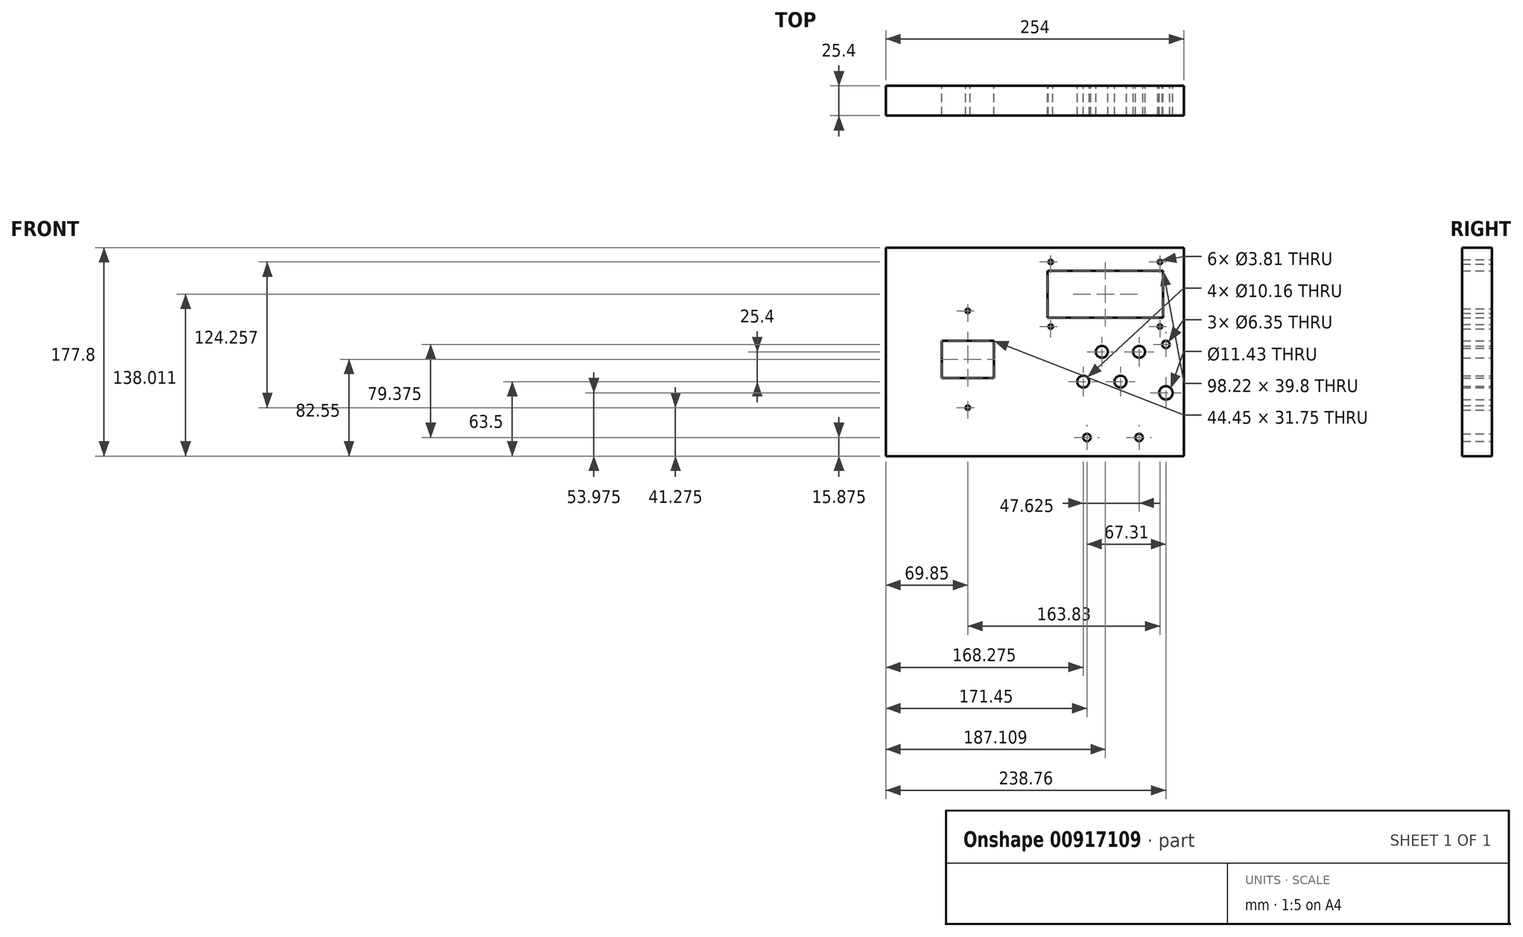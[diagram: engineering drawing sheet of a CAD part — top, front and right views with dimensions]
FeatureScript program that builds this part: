
annotation { "Feature Type Name" : "Feature", "Feature Type Description" : "" }
export const myFeature = defineFeature(function(context is Context, id is Id, definition is map)
    precondition{}
    {
        {
            var Q0;
            Q0=qCreatedBy(makeId("Front.planeOp"),FACE);
            var sketch = newSketch(context, id + "F0", { "sketchPlane" : qUnion([Q0])});
            skLineSegment(sketch, "E0.bottom", {"start": v(0, 0) * mm, "end": v(254, 0) * mm});
            skLineSegment(sketch, "E0.top", {"start": v(0, -177.8) * mm, "end": v(254, -177.8) * mm});
            skLineSegment(sketch, "E0.left", {"start": v(0, 0) * mm, "end": v(0, -177.8) * mm});
            skLineSegment(sketch, "E0.right", {"start": v(254, 0) * mm, "end": v(254, -177.8) * mm});
            skLineSegment(sketch, "E1.bottom", {"start": v(0, 0) * mm, "end": v(17.78, 0) * mm});
            skLineSegment(sketch, "E1.top", {"start": v(5.08, -17.78) * mm, "end": v(17.78, -17.78) * mm, "construction": true});
            skLineSegment(sketch, "E1.left", {"start": v(0, 0) * mm, "end": v(0, -17.78) * mm});
            skLineSegment(sketch, "E1.right", {"start": v(17.78, -5.08) * mm, "end": v(17.78, -17.78) * mm, "construction": true});
            skLineSegment(sketch, "E2.bottom", {"start": v(254, 0) * mm, "end": v(236.22, 0) * mm});
            skLineSegment(sketch, "E2.top", {"start": v(248.92, -17.78) * mm, "end": v(236.22, -17.78) * mm, "construction": true});
            skLineSegment(sketch, "E2.left", {"start": v(254, 0) * mm, "end": v(254, -17.78) * mm});
            skLineSegment(sketch, "E2.right", {"start": v(236.22, -5.08) * mm, "end": v(236.22, -17.78) * mm, "construction": true});
            skLineSegment(sketch, "E3.bottom", {"start": v(0, -177.8) * mm, "end": v(17.78, -177.8) * mm});
            skLineSegment(sketch, "E3.top", {"start": v(5.08, -160.02) * mm, "end": v(17.78, -160.02) * mm, "construction": true});
            skLineSegment(sketch, "E3.left", {"start": v(0, -177.8) * mm, "end": v(0, -160.02) * mm});
            skLineSegment(sketch, "E3.right", {"start": v(17.78, -172.72) * mm, "end": v(17.78, -160.02) * mm, "construction": true});
            skLineSegment(sketch, "E4.bottom", {"start": v(254, -177.8) * mm, "end": v(236.22, -177.8) * mm});
            skLineSegment(sketch, "E4.top", {"start": v(248.92, -160.02) * mm, "end": v(236.22, -160.02) * mm, "construction": true});
            skLineSegment(sketch, "E4.left", {"start": v(254, -177.8) * mm, "end": v(254, -160.02) * mm});
            skLineSegment(sketch, "E4.right", {"start": v(236.22, -172.72) * mm, "end": v(236.22, -160.02) * mm, "construction": true});
            skLineSegment(sketch, "E5.bottom", {"start": v(0, 0) * mm, "end": v(139.7, 0) * mm});
            skLineSegment(sketch, "E5.top", {"start": v(0, -177.8) * mm, "end": v(139.7, -177.8) * mm});
            skLineSegment(sketch, "E5.right", {"start": v(139.7, -69.85) * mm, "end": v(139.7, -177.8) * mm, "construction": true});
            skCircle(sketch, "E6", {"center": v(69.85, -136.53) * mm, "radius": 1.9 * mm});
            skCircle(sketch, "E7", {"center": v(69.85, -53.97) * mm, "radius": 1.9 * mm});
            skLineSegment(sketch, "E8.bottom", {"start": v(254, -177.8) * mm, "end": v(228.6, -177.8) * mm});
            skLineSegment(sketch, "E8.top", {"start": v(254, -95.25) * mm, "end": v(228.6, -95.25) * mm, "construction": true});
            skLineSegment(sketch, "E8.left", {"start": v(254, -177.8) * mm, "end": v(254, -95.25) * mm});
            skLineSegment(sketch, "E9.bottom", {"start": v(139.7, -177.8) * mm, "end": v(228.6, -177.8) * mm});
            skLineSegment(sketch, "E9.top", {"start": v(139.7, -146.05) * mm, "end": v(228.6, -146.05) * mm, "construction": true});
            skLineSegment(sketch, "E9.left", {"start": v(139.7, -177.8) * mm, "end": v(139.7, -146.05) * mm});
            skLineSegment(sketch, "E9.right", {"start": v(228.6, -177.8) * mm, "end": v(228.6, -146.05) * mm, "construction": true});
            skLineSegment(sketch, "E10", {"start": v(139.7, -127) * mm, "end": v(228.6, -127) * mm, "construction": true});
            skPoint(sketch, "E11.endSnap0", {"position": v(254, -88.9) * mm});
            skLineSegment(sketch, "E12", {"start": v(228.6, -95.25) * mm, "end": v(228.6, -69.85) * mm, "construction": true});
            skLineSegment(sketch, "E13.left", {"start": v(236.22, -9.73) * mm, "end": v(236.22, -69.85) * mm});
            skLineSegment(sketch, "E14.bottom", {"start": v(5.08, -5.08) * mm, "end": v(248.92, -5.08) * mm, "construction": true});
            skLineSegment(sketch, "E14.top", {"start": v(5.08, -172.72) * mm, "end": v(248.92, -172.72) * mm, "construction": true});
            skLineSegment(sketch, "E14.left", {"start": v(5.08, -5.08) * mm, "end": v(5.08, -172.72) * mm, "construction": true});
            skLineSegment(sketch, "E14.right", {"start": v(248.92, -5.08) * mm, "end": v(248.92, -172.72) * mm, "construction": true});
            skCircle(sketch, "E15", {"center": v(140.54, -12.27) * mm, "radius": 1.9 * mm});
            skCircle(sketch, "E16", {"center": v(233.68, -12.27) * mm, "radius": 1.9 * mm});
            skCircle(sketch, "E17", {"center": v(233.68, -67.3) * mm, "radius": 1.9 * mm});
            skCircle(sketch, "E18", {"center": v(140.54, -67.3) * mm, "radius": 1.9 * mm});
            skLineSegment(sketch, "E19", {"start": v(138, -59.7) * mm, "end": v(236.22, -59.69) * mm});
            skLineSegment(sketch, "E20", {"start": v(138, -19.89) * mm, "end": v(236.22, -19.89) * mm});
            skLineSegment(sketch, "E21", {"start": v(69.85, -53.97) * mm, "end": v(69.85, -136.53) * mm, "construction": true});
            skLineSegment(sketch, "E22.bottom", {"start": v(47.62, -79.37) * mm, "end": v(92.07, -79.37) * mm});
            skLineSegment(sketch, "E22.top", {"start": v(47.62, -111.12) * mm, "end": v(92.07, -111.12) * mm});
            skLineSegment(sketch, "E22.left", {"start": v(47.62, -79.37) * mm, "end": v(47.62, -111.12) * mm});
            skLineSegment(sketch, "E22.right", {"start": v(92.07, -79.37) * mm, "end": v(92.07, -111.12) * mm});
            skCircle(sketch, "E23", {"center": v(215.9, -88.9) * mm, "radius": 5.08 * mm});
            skCircle(sketch, "E24", {"center": v(200.03, -114.3) * mm, "radius": 5.08 * mm});
            skCircle(sketch, "E25", {"center": v(168.28, -114.3) * mm, "radius": 5.08 * mm});
            skCircle(sketch, "E26", {"center": v(184.15, -88.9) * mm, "radius": 5.08 * mm});
            skLineSegment(sketch, "E27", {"start": v(236.22, -160.02) * mm, "end": v(228.6, -160.02) * mm, "construction": true});
            skLineSegment(sketch, "E28", {"start": v(138, -69.85) * mm, "end": v(254, -69.85) * mm, "construction": true});
            skLineSegment(sketch, "E29", {"start": v(138, -9.73) * mm, "end": v(236.22, -9.73) * mm, "construction": true});
            skLineSegment(sketch, "E30", {"start": v(138, -19.89) * mm, "end": v(138, -59.69) * mm});
            skLineSegment(sketch, "E31", {"start": v(138, -69.85) * mm, "end": v(138, -59.69) * mm, "construction": true});
            skLineSegment(sketch, "E32", {"start": v(138, -9.73) * mm, "end": v(138, -19.89) * mm, "construction": true});
            skLineSegment(sketch, "E33", {"start": v(228.6, -95.25) * mm, "end": v(228.6, -146.05) * mm, "construction": true});
            skCircle(sketch, "E34", {"center": v(238.76, -123.82) * mm, "radius": 5.72 * mm});
            skCircle(sketch, "E35", {"center": v(171.45, -161.92) * mm, "radius": 3.18 * mm});
            skCircle(sketch, "E36", {"center": v(215.9, -161.92) * mm, "radius": 3.18 * mm});
            skCircle(sketch, "E37", {"center": v(238.76, -82.55) * mm, "radius": 3.18 * mm});
            skSolve(sketch);
        }
        {
            var Q0;
            {var subQ9=sQuery(id+"F0.wireOp",EDGE,"E0.right");Q0=makeQuery(id+"F0.imprint","IMPRINT",FACE,{"disambiguationData":[TD([[makeQuery(id+"F0.imprint","IMPRINT",EDGE,{"derivedFrom":subQ9}),-1.0]])]});}
            var Q1;
            {var subQ2=sQuery(id+"F0.wireOp",EDGE,"E0.right");Q1=makeQuery(id+"F0.imprint","IMPRINT",FACE,{"disambiguationData":[TD([[makeQuery(id+"F0.imprint","IMPRINT",EDGE,{"derivedFrom":subQ2}),1.0]])]});}
            extrude(context, id + "F1", {"entities" : qUnion([Q0, Q1]), "depth" : 25.4 * mm, "offsetDistance" : 25.4 * mm});
        }
    });
